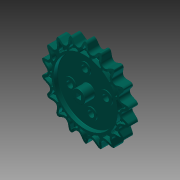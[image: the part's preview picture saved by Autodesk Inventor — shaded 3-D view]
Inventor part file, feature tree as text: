
AUTODESK INVENTOR PART (.ipt)
format: ipt  version: 2013 (Build 170138000, 138)  size: 1,626,112 bytes
history: native  units: in
note: dims shown in document units (in); Inventor stores cm internally (conversion verified against a paired STEP export)
features: sketch x9, extrude x7, projected_geometry x4, fillet x2, revolve x1, pattern_circular x1, mirror x1, hole x1, other x1
ambient origin geometry x8: Origin, YZ Plane, XZ Plane, XY Plane, X Axis, Y Axis, Z Axis, Center Point
bodies: Solid1 (feature_tree)
feature tree (27):
  sketch  "Sketch1"  dims[d0=0.3in d1=0.0in d2=1.693in]
  extrude  "Extrusion1"  Depth=1.693in
  extrude  "Extrusion2"  Depth=0.354in
  extrude  "Extrusion3"  Depth=2.112in
  sketch  "Sketch4"  dims[d11=90.0deg d12=0.029in]
  revolve  "Revolution1"  [1 undecoded]
  extrude  "Extrusion4"  Depth=0.111in TaperAngle=0.0deg
  fillet  "Fillet1"  Radius=0.012in
  fillet  "Fillet2"  Radius=0.012in
  pattern_circular  "Circular Pattern1"  Count=18 Angle=360.0deg
  extrude  "Extrusion5"  Depth=0.5in
  mirror  "Mirror1"
  hole  "Hole1"  [1 undecoded]
  extrude  "Extrusion6"  Depth=0.315in
  sketch  "Sketch2"  dims[d3=0.111in d4=0.0in d5=0.354in]
  sketch  "Sketch3"  dims[d6=0.273in d7=0.0in d8=2.112in]
  sketch  "Sketch5"  dims[d13=0.165in d15=0.111in d16=0.0in d17=0.012in d18=0.012in d19=7.0866in d20=360.0deg]
  sketch  "Sketch6"  dims[d25=0.5in d26=0.5in]
  sketch  "Sketch7"  dims[d27=0.5in d29=0.5in]
  projected_geometry  "Projected Loop1"
  sketch  "Sketch8"  dims[d30=0.5in d31=0.315in]
  projected_geometry  "Projected Loop2"
  projected_geometry  "Projected Loop3"
  projected_geometry  "Projected Loop4"
  sketch  "Sketch9"  dims[d32=0.315in d33=0.354in d34=0.354in d35=0.023in d36=0.0in d37=0.175in d38=0.75in d39=0.375in d40=0.25in d41=0.5635in d42=1.0in d43=0.8108in d44=0.023in d45=0.0in d46=0.477in d47=0.0in d48=0.0in d49=0.0in]
  other  "Srf1"
  extrude  "ExtrusionSrf1"  Depth=0.354in
note: 2 required parameter values undecoded (feature->parameter linkage not recoverable at this tier; creation-order binding heuristic only, values carry confidence <= 0.55)